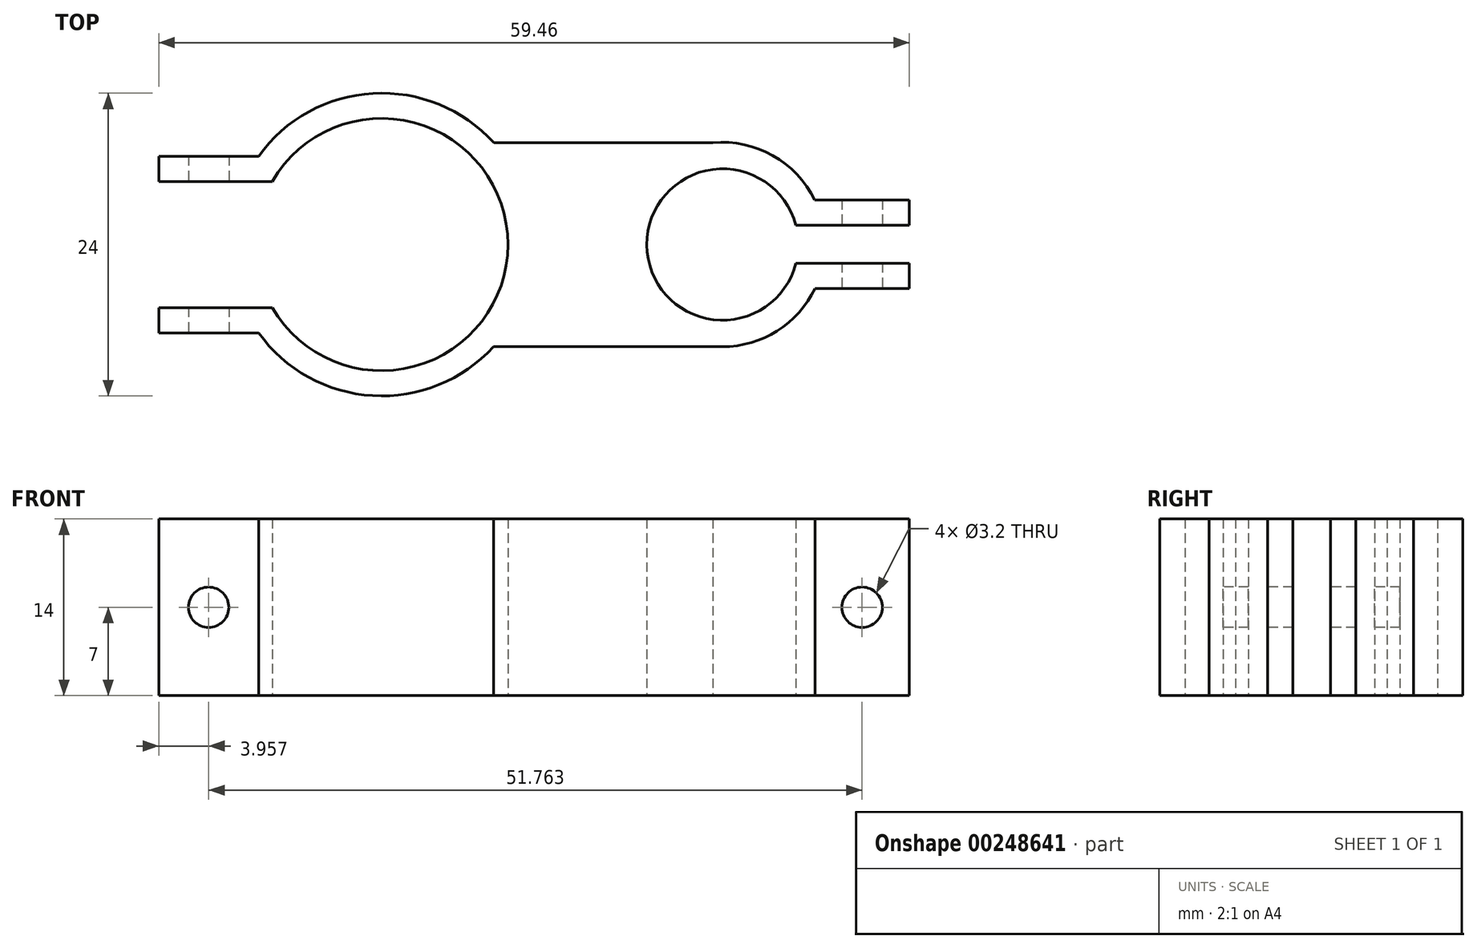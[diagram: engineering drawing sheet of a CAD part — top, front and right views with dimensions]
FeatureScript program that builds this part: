
annotation { "Feature Type Name" : "Feature", "Feature Type Description" : "" }
export const myFeature = defineFeature(function(context is Context, id is Id, definition is map)
    precondition{}
    {
        {
            var Q0;
            Q0=qCreatedBy(makeId("Top.planeOp"),FACE);
            var sketch = newSketch(context, id + "F0", { "sketchPlane" : qUnion([Q0])});
            skArc(sketch, "E0", {"start": v(-71.98, 26.18) * mm, "mid": v(-53.32, 31.18) * mm, "end": v(-71.98, 36.18) * mm});
            skArc(sketch, "E1", {"start": v(-30.52, 32.7) * mm, "mid": v(-42.32, 31.16) * mm, "end": v(-30.5, 29.7) * mm});
            skLineSegment(sketch, "E2", {"start": v(-63.32, 31.18) * mm, "end": v(-36.32, 31.18) * mm, "construction": true});
            skArc(sketch, "E3", {"start": v(-73.07, 24.18) * mm, "mid": v(-64.03, 19.2) * mm, "end": v(-54.47, 23.08) * mm});
            skArc(sketch, "E4", {"start": v(-29.03, 34.7) * mm, "mid": v(-32.34, 38.24) * mm, "end": v(-37.08, 39.25) * mm});
            skLineSegment(sketch, "E5.top", {"start": v(-71.98, 36.18) * mm, "end": v(-80.98, 36.18) * mm});
            skLineSegment(sketch, "E5.right", {"start": v(-80.98, 38.18) * mm, "end": v(-80.98, 36.18) * mm});
            skLineSegment(sketch, "E6.bottom", {"start": v(-71.98, 26.18) * mm, "end": v(-80.98, 26.18) * mm});
            skLineSegment(sketch, "E6.top", {"start": v(-73.07, 24.18) * mm, "end": v(-80.98, 24.18) * mm});
            skLineSegment(sketch, "E6.right", {"start": v(-80.98, 26.18) * mm, "end": v(-80.98, 24.18) * mm});
            skLineSegment(sketch, "E7", {"start": v(-80.98, 36.18) * mm, "end": v(-80.98, 26.18) * mm, "construction": true});
            skPoint(sketch, "E8", {"position": v(-80.98, 31.18) * mm});
            skLineSegment(sketch, "E9.trimOffspring", {"start": v(-73.07, 38.18) * mm, "end": v(-80.98, 38.18) * mm});
            skLineSegment(sketch, "E10", {"start": v(-36.32, 23.08) * mm, "end": v(-54.47, 23.08) * mm});
            skLineSegment(sketch, "E11", {"start": v(-36.32, 39.25) * mm, "end": v(-54.43, 39.25) * mm});
            skLineSegment(sketch, "E12.bottom", {"start": v(-21.52, 29.7) * mm, "end": v(-30.5, 29.7) * mm});
            skLineSegment(sketch, "E12.top", {"start": v(-21.52, 32.7) * mm, "end": v(-30.52, 32.7) * mm});
            skLineSegment(sketch, "E13.bottom", {"start": v(-21.52, 27.7) * mm, "end": v(-29, 27.7) * mm});
            skLineSegment(sketch, "E13.top", {"start": v(-21.52, 34.7) * mm, "end": v(-29.03, 34.7) * mm});
            skLineSegment(sketch, "E13.left", {"start": v(-21.52, 27.7) * mm, "end": v(-21.52, 29.7) * mm});
            skLineSegment(sketch, "E14.trimOffspring", {"start": v(-21.52, 32.7) * mm, "end": v(-21.52, 34.7) * mm});
            skArc(sketch, "E15.trimOffspring", {"start": v(-54.43, 39.25) * mm, "mid": v(-64, 43.16) * mm, "end": v(-73.07, 38.18) * mm});
            skArc(sketch, "E16.trimOffspring", {"start": v(-36.32, 23.08) * mm, "mid": v(-32, 24.33) * mm, "end": v(-29, 27.7) * mm});
            skSolve(sketch);
        }
        {
            var Q0;
            Q0 = qSketchRegion(id + "F0", true);
            extrude(context, id + "F1", {"entities" : qUnion([Q0]), "depth" : 14 * mm, "offsetDistance" : 25 * mm});
        }
        {
            var Q0;
            Q0=makeQuery(id+"F1.opExtrude","SWEPT_FACE",FACE,{"disambiguationData":[OSD([sQuery(id+"F0.wireOp",EDGE,"E6.top")])]});
            var sketch = newSketch(context, id + "F2", { "sketchPlane" : qUnion([Q0])});
            skLineSegment(sketch, "E17", {"start": v(-80.98, 0) * mm, "end": v(-73.07, 14) * mm, "construction": true});
            skCircle(sketch, "E18", {"center": v(-77.02, 7) * mm, "radius": 1.6 * mm});
            skLineSegment(sketch, "E19", {"start": v(-21.52, 14) * mm, "end": v(-29, 0) * mm, "construction": true});
            skPoint(sketch, "E20", {"position": v(-25.26, 7) * mm});
            skCircle(sketch, "E21", {"center": v(-25.26, 7) * mm, "radius": 1.6 * mm});
            skSolve(sketch);
        }
        {
            var Q0;
            Q0=makeQuery(id+"F2.imprint","IMPRINT",FACE,{"disambiguationData":[TD([[makeQuery(id+"F2.imprint","IMPRINT",EDGE,{"derivedFrom":sQuery(id+"F2.wireOp",EDGE,"E18")}),1.0]])]});
            var Q1;
            Q1=makeQuery(id+"F2.imprint","IMPRINT",FACE,{"disambiguationData":[TD([[makeQuery(id+"F2.imprint","IMPRINT",EDGE,{"derivedFrom":sQuery(id+"F2.wireOp",EDGE,"E21")}),1.0]])]});
            extrude(context, id + "F3", {"entities" : qUnion([Q0, Q1]), "operationType" : NewBodyOperationType.REMOVE, "endBound" : BoundingType.THROUGH_ALL, "oppositeDirection" : true, "depth" : 25 * mm, "offsetDistance" : 25 * mm});
        }
    });
